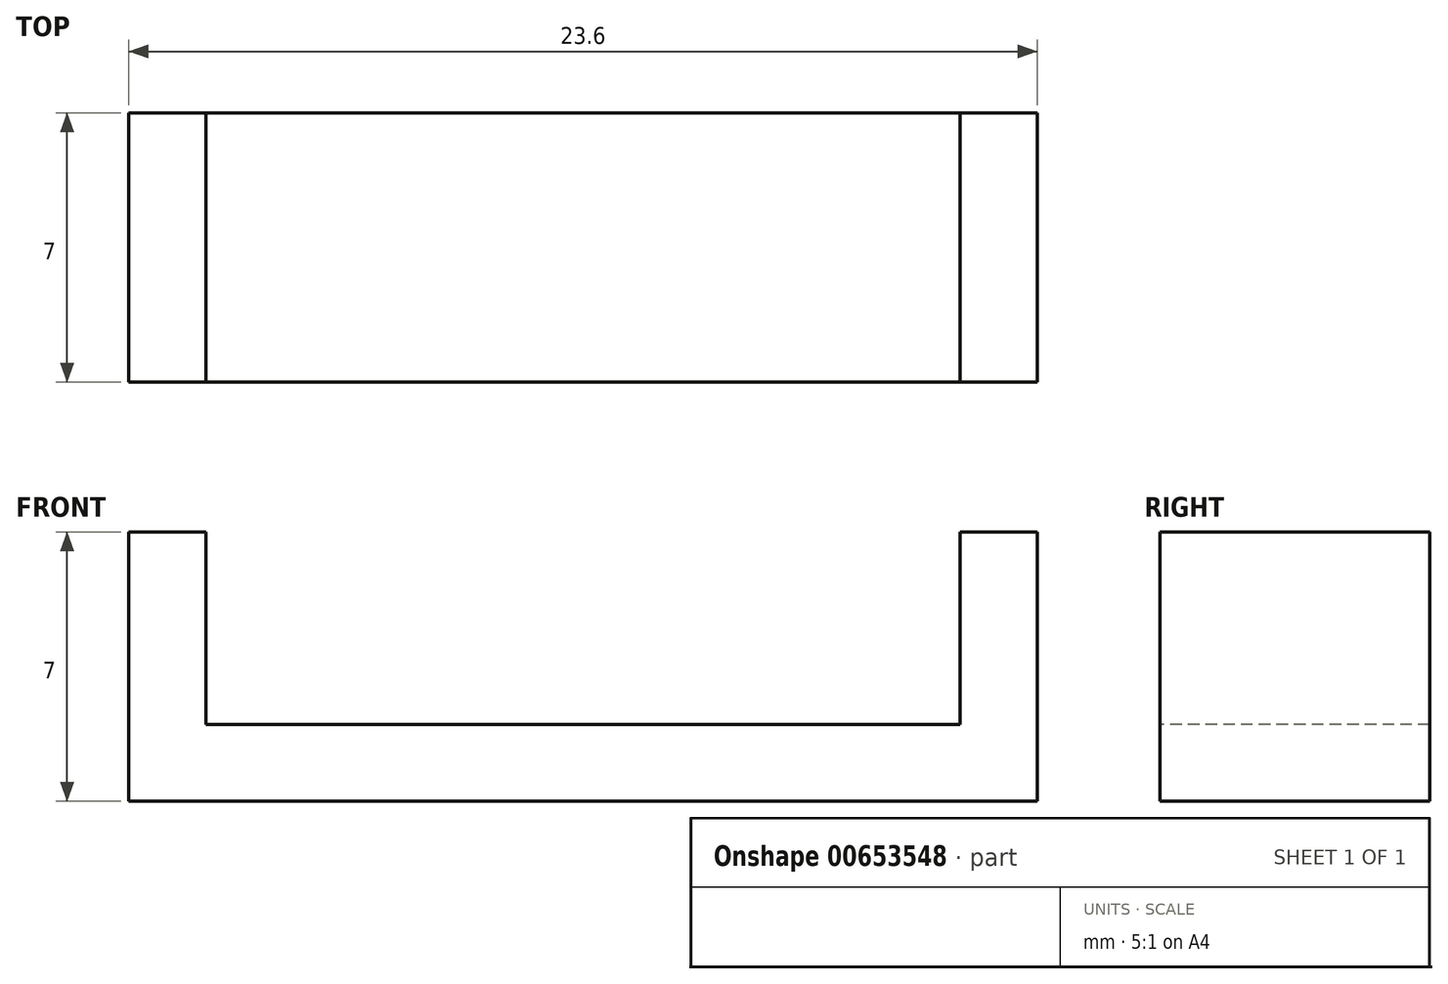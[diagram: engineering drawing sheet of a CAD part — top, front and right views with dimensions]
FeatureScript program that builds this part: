
annotation { "Feature Type Name" : "Feature", "Feature Type Description" : "" }
export const myFeature = defineFeature(function(context is Context, id is Id, definition is map)
    precondition{}
    {
        {
            var Q0;
            Q0=qCreatedBy(makeId("Front.planeOp"),FACE);
            var sketch = newSketch(context, id + "F0", { "sketchPlane" : qUnion([Q0])});
            skLineSegment(sketch, "E0", {"start": v(0, 0) * mm, "end": v(11.8, 0) * mm});
            skLineSegment(sketch, "E1", {"start": v(11.8, 0) * mm, "end": v(11.8, 7) * mm});
            skLineSegment(sketch, "E2", {"start": v(11.8, 7) * mm, "end": v(9.8, 7) * mm});
            skLineSegment(sketch, "E3", {"start": v(9.8, 7) * mm, "end": v(9.8, 2) * mm});
            skLineSegment(sketch, "E4", {"start": v(9.8, 2) * mm, "end": v(0, 2) * mm});
            skLineSegment(sketch, "E5", {"start": v(0, 2) * mm, "end": v(0, 0) * mm});
            skSolve(sketch);
        }
        {
            var Q0;
            Q0=makeQuery(id+"F0.imprint","IMPRINT",FACE,{"disambiguationData":[TD([[makeQuery(id+"F0.imprint","IMPRINT",EDGE,{"derivedFrom":sQuery(id+"F0.wireOp",EDGE,"E0")}),1.0]])]});
            extrude(context, id + "F1", {"entities" : qUnion([Q0]), "oppositeDirection" : true, "depth" : 7 * mm, "offsetDistance" : 25 * mm});
        }
        {
            var Q0;
            Q0=makeQuery(id+"F1.opExtrude","SWEPT_BODY",BODY,{"disambiguationData":[OSD([sQuery(id+"F0.wireOp",EDGE,"E0"),sQuery(id+"F0.wireOp",EDGE,"E1"),sQuery(id+"F0.wireOp",EDGE,"E2"),sQuery(id+"F0.wireOp",EDGE,"E3"),sQuery(id+"F0.wireOp",EDGE,"E4"),sQuery(id+"F0.wireOp",EDGE,"E5")])]});
            var Q1;
            Q1=qCreatedBy(makeId("Right.planeOp"),FACE);
            mirror(context, id + "F2", {"operationType" : NewBodyOperationType.ADD, "entities" : qUnion([Q0]), "mirrorPlane" : qUnion([Q1])});
        }
    });
